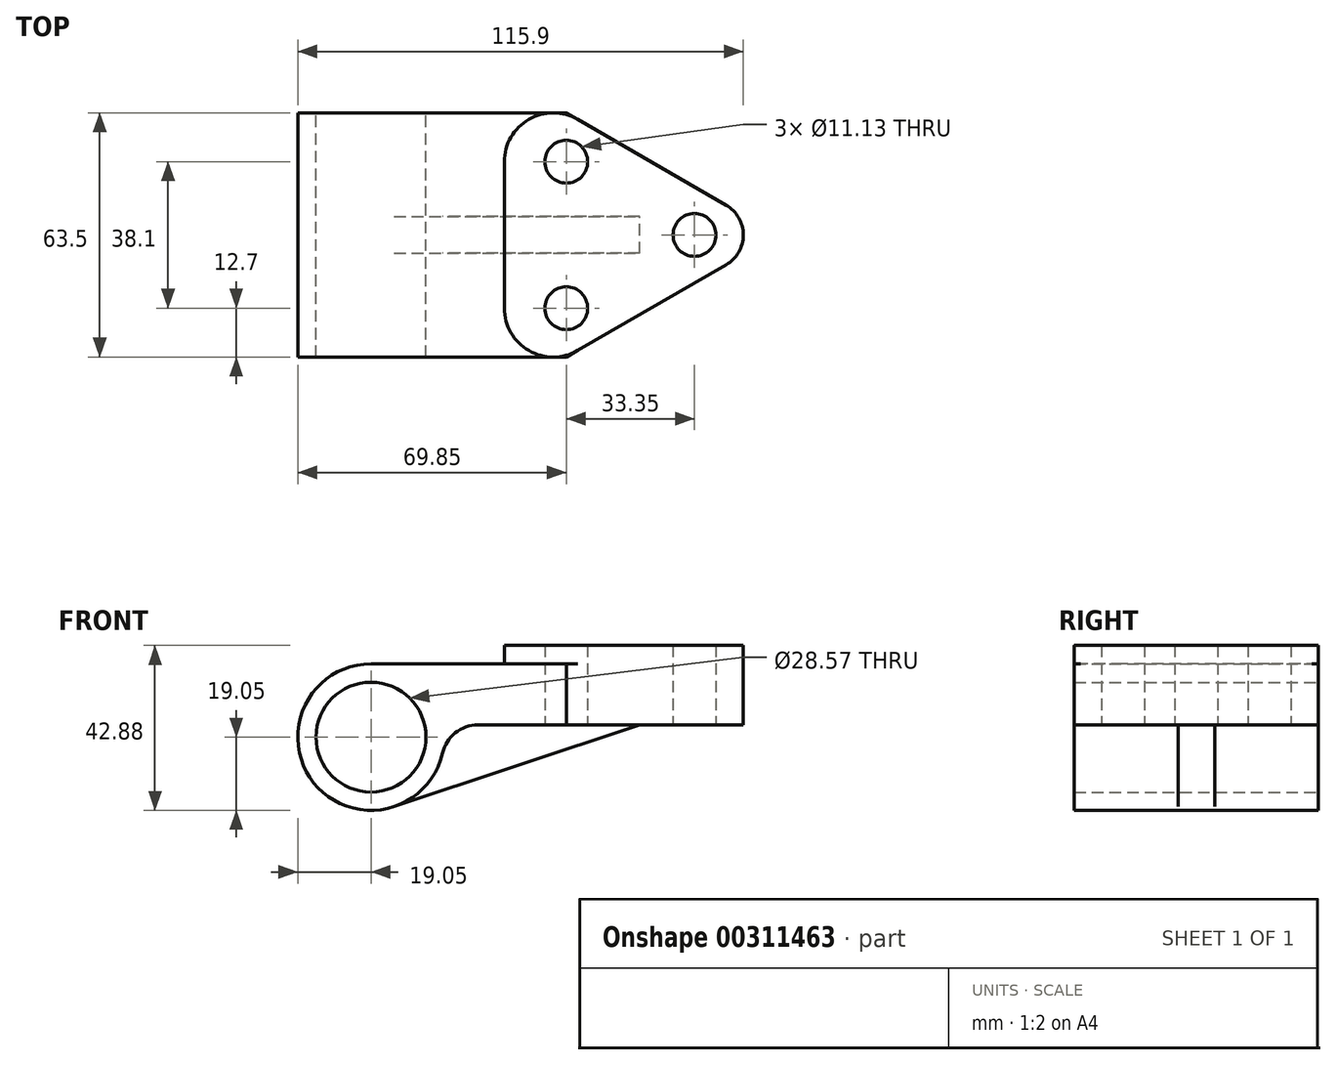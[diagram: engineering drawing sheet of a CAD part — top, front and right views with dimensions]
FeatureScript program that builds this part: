
annotation { "Feature Type Name" : "Feature", "Feature Type Description" : "" }
export const myFeature = defineFeature(function(context is Context, id is Id, definition is map)
    precondition{}
    {
        {
            var Q0;
            Q0=qCreatedBy(makeId("Front.planeOp"),FACE);
            var sketch = newSketch(context, id + "F0", { "sketchPlane" : qUnion([Q0])});
            skCircle(sketch, "E0", {"center": v(0, 0) * mm, "radius": 19.05 * mm});
            skCircle(sketch, "E1", {"center": v(0, 0) * mm, "radius": 14.29 * mm});
            skLineSegment(sketch, "E2", {"start": v(96.85, 3.18) * mm, "end": v(96.85, 19.05) * mm});
            skLineSegment(sketch, "E3", {"start": v(96.85, 19.05) * mm, "end": v(0, 19.05) * mm});
            skLineSegment(sketch, "E4", {"start": v(96.85, 3.18) * mm, "end": v(18.78, 3.18) * mm});
            skArc(sketch, "E5", {"start": v(27.86, 3.18) * mm, "mid": v(21.92, 1.1) * mm, "end": v(18.57, -4.23) * mm});
            skLineSegment(sketch, "E6", {"start": v(6.02, -18.07) * mm, "end": v(69.85, 3.18) * mm});
            skSolve(sketch);
        }
        {
            var Q0;
            {var subQ1=sQuery(id+"F0.wireOp",EDGE,"E2");Q0=makeQuery(id+"F0.imprint","IMPRINT",FACE,{"disambiguationData":[TD([[makeQuery(id+"F0.imprint","IMPRINT",EDGE,{"derivedFrom":subQ1}),1.0]])]});}
            var Q1;
            Q1=makeQuery(id+"F0.imprint","IMPRINT",FACE,{"disambiguationData":[TD([[makeQuery(id+"F0.imprint","IMPRINT",EDGE,{"derivedFrom":sQuery(id+"F0.wireOp",EDGE,"E1")}),-1.0]])]});
            var Q2;
            {var subQ3=sQuery(id+"F0.wireOp",EDGE,"E5");Q2=makeQuery(id+"F0.imprint","IMPRINT",FACE,{"disambiguationData":[TD([[makeQuery(id+"F0.imprint","IMPRINT",EDGE,{"derivedFrom":subQ3}),-1.0]])]});}
            extrude(context, id + "F1", {"entities" : qUnion([Q0, Q1, Q2]), "endBound" : BoundingType.SYMMETRIC, "depth" : 63.5 * mm});
        }
        {
            var Q0;
            {var subQ0=sQuery(id+"F0.wireOp",EDGE,"E5");Q0=makeQuery(id+"F0.imprint","IMPRINT",FACE,{"disambiguationData":[TD([[makeQuery(id+"F0.imprint","IMPRINT",EDGE,{"derivedFrom":subQ0}),1.0]])]});}
            extrude(context, id + "F2", {"entities" : qUnion([Q0]), "operationType" : NewBodyOperationType.ADD, "endBound" : BoundingType.SYMMETRIC, "depth" : 9.52 * mm});
        }
        {
            var Q0;
            Q0=makeQuery(id+"F1.opExtrude","SWEPT_FACE",FACE,{"disambiguationData":[OSD([sQuery(id+"F0.wireOp",EDGE,"E3")])]});
            var sketch = newSketch(context, id + "F3", { "sketchPlane" : qUnion([Q0])});
            skLineSegment(sketch, "E7", {"start": v(96.85, 0) * mm, "end": v(0, 0) * mm, "construction": true});
            skLineSegment(sketch, "E8", {"start": v(84.15, 31.75) * mm, "end": v(84.15, -31.75) * mm, "construction": true});
            skLineSegment(sketch, "E9", {"start": v(50.8, 31.75) * mm, "end": v(50.8, -31.75) * mm, "construction": true});
            skLineSegment(sketch, "E10", {"start": v(68.2, -19.05) * mm, "end": v(34.78, -19.05) * mm, "construction": true});
            skLineSegment(sketch, "E11", {"start": v(64.41, 19.05) * mm, "end": v(33.79, 19.05) * mm, "construction": true});
            skLineSegment(sketch, "E12", {"start": v(50.8, -31.75) * mm, "end": v(96.85, -5.16) * mm});
            skLineSegment(sketch, "E13", {"start": v(50.8, 31.75) * mm, "end": v(96.85, 5.16) * mm});
            skArc(sketch, "E14", {"start": v(92.38, -7.74) * mm, "mid": v(96.85, 0) * mm, "end": v(92.38, 7.74) * mm});
            skLineSegment(sketch, "E15", {"start": v(34.7, 31.75) * mm, "end": v(34.7, -31.75) * mm});
            skArc(sketch, "E16", {"start": v(53.75, 30.05) * mm, "mid": v(41.05, 30.05) * mm, "end": v(34.7, 19.05) * mm});
            skArc(sketch, "E17", {"start": v(34.7, -19.05) * mm, "mid": v(41.05, -30.05) * mm, "end": v(53.75, -30.05) * mm});
            skCircle(sketch, "E18", {"center": v(84.15, 0) * mm, "radius": 5.56 * mm});
            skCircle(sketch, "E19", {"center": v(50.8, -19.05) * mm, "radius": 5.56 * mm});
            skCircle(sketch, "E20", {"center": v(50.8, 19.05) * mm, "radius": 5.56 * mm});
            skSolve(sketch);
        }
        {
            var Q0;
            Q0=makeQuery(id+"F3.imprint","IMPRINT",FACE,{"disambiguationData":[TD([[makeQuery(id+"F3.imprint","IMPRINT",EDGE,{"derivedFrom":sQuery(id+"F3.wireOp",EDGE,"E18")}),-1.0]])]});
            extrude(context, id + "F4", {"entities" : qUnion([Q0]), "operationType" : NewBodyOperationType.ADD, "depth" : 4.78 * mm});
        }
        {
            var Q0;
            {var subQ0=sQuery(id+"F3.wireOp",EDGE,"E12");var subQ1=sQuery(id+"F0.wireOp",EDGE,"E3");var subQ6=makeQuery(id+"F1.opExtrude","CAP_EDGE",EDGE,{"disambiguationData":[OSD([subQ1])],"isStart":false});var subQ8=makeQuery(id+"F3.imprint","INTERSECT",VERTEX,{"derivedFrom":[subQ6,subQ0]});Q0=makeQuery(id+"F3.imprint","IMPRINT",FACE,{"disambiguationData":[TD([[makeQuery(id+"F3.imprint","IMPRINT",EDGE,{"disambiguationData":[TD([[subQ8,-1.0]])],"derivedFrom":subQ0}),-1.0]])]});}
            var Q1;
            {var subQ0=sQuery(id+"F3.wireOp",EDGE,"E13");var subQ1=sQuery(id+"F0.wireOp",EDGE,"E3");var subQ5=makeQuery(id+"F1.opExtrude","CAP_EDGE",EDGE,{"disambiguationData":[OSD([subQ1])],"isStart":true});var subQ8=makeQuery(id+"F3.imprint","INTERSECT",VERTEX,{"derivedFrom":[subQ5,subQ0]});Q1=makeQuery(id+"F3.imprint","IMPRINT",FACE,{"disambiguationData":[TD([[makeQuery(id+"F3.imprint","IMPRINT",EDGE,{"disambiguationData":[TD([[subQ8,-1.0]])],"derivedFrom":subQ0}),1.0]])]});}
            var Q2;
            {var subQ0=sQuery(id+"F3.wireOp",EDGE,"E13");var subQ3=sQuery(id+"F3.wireOp",EDGE,"E14");var subQ4=makeQuery(id+"F3.imprint","INTERSECT",VERTEX,{"derivedFrom":[subQ0,subQ3]});Q2=makeQuery(id+"F3.imprint","IMPRINT",FACE,{"disambiguationData":[TD([[makeQuery(id+"F3.imprint","IMPRINT",EDGE,{"disambiguationData":[TD([[subQ4,-1.0]])],"derivedFrom":subQ0}),-1.0]])]});}
            var Q3;
            {var subQ0=sQuery(id+"F3.wireOp",EDGE,"E12");var subQ3=sQuery(id+"F3.wireOp",EDGE,"E14");var subQ4=makeQuery(id+"F3.imprint","INTERSECT",VERTEX,{"derivedFrom":[subQ0,subQ3]});Q3=makeQuery(id+"F3.imprint","IMPRINT",FACE,{"disambiguationData":[TD([[makeQuery(id+"F3.imprint","IMPRINT",EDGE,{"disambiguationData":[TD([[subQ4,-1.0]])],"derivedFrom":subQ0}),1.0]])]});}
            var Q4;
            Q4=makeQuery(id+"F1.opExtrude","SWEPT_FACE",FACE,{"disambiguationData":[OSD([sQuery(id+"F0.wireOp",EDGE,"E4")])]});
            extrude(context, id + "F5", {"entities" : qUnion([Q0, Q1, Q2, Q3]), "operationType" : NewBodyOperationType.REMOVE, "endBound" : BoundingType.UP_TO_SURFACE, "oppositeDirection" : true, "endBoundEntityFace" : qUnion([Q4]), "depth" : 25.4 * mm});
        }
        {
            var Q0;
            Q0=makeQuery(id+"F3.imprint","IMPRINT",FACE,{"disambiguationData":[TD([[makeQuery(id+"F3.imprint","IMPRINT",EDGE,{"derivedFrom":sQuery(id+"F3.wireOp",EDGE,"E18")}),1.0]])]});
            var Q1;
            Q1=makeQuery(id+"F3.imprint","IMPRINT",FACE,{"disambiguationData":[TD([[makeQuery(id+"F3.imprint","IMPRINT",EDGE,{"derivedFrom":sQuery(id+"F3.wireOp",EDGE,"E20")}),1.0]])]});
            var Q2;
            Q2=makeQuery(id+"F3.imprint","IMPRINT",FACE,{"disambiguationData":[TD([[makeQuery(id+"F3.imprint","IMPRINT",EDGE,{"derivedFrom":sQuery(id+"F3.wireOp",EDGE,"E19")}),1.0]])]});
            var Q3;
            Q3=makeQuery(id+"F1.opExtrude","SWEPT_FACE",FACE,{"disambiguationData":[OSD([sQuery(id+"F0.wireOp",EDGE,"E4")])]});
            extrude(context, id + "F6", {"entities" : qUnion([Q0, Q1, Q2]), "operationType" : NewBodyOperationType.REMOVE, "endBound" : BoundingType.UP_TO_SURFACE, "oppositeDirection" : true, "endBoundEntityFace" : qUnion([Q3]), "depth" : 25.4 * mm});
        }
    });
